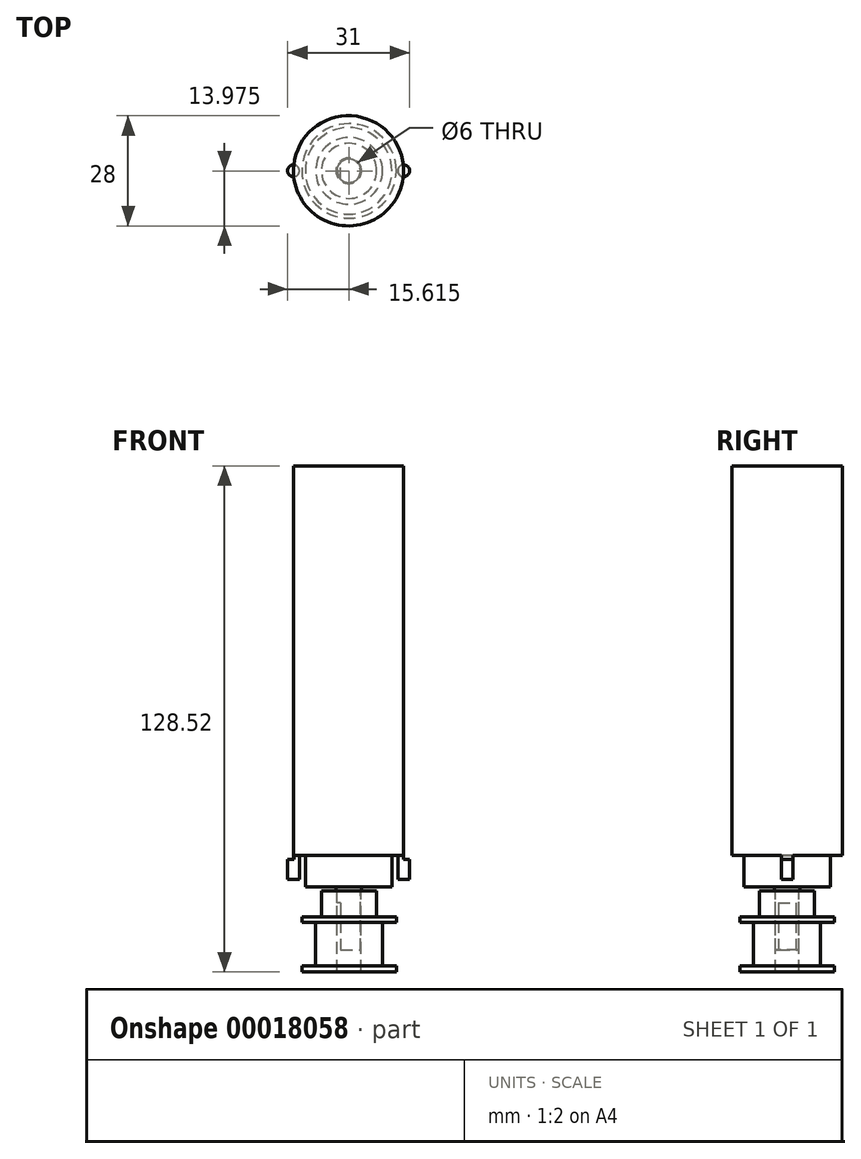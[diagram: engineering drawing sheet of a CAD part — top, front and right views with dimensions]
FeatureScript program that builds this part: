
annotation { "Feature Type Name" : "Feature", "Feature Type Description" : "" }
export const myFeature = defineFeature(function(context is Context, id is Id, definition is map)
    precondition{}
    {
        {
            var Q0;
            Q0=qCreatedBy(makeId("Top.planeOp"),FACE);
            var sketch = newSketch(context, id + "F0", { "sketchPlane" : qUnion([Q0])});
            skCircle(sketch, "E0", {"center": v(0, 0) * mm, "radius": 14 * mm});
            skCircle(sketch, "E1", {"center": v(0, 0) * mm, "radius": 18 * mm});
            skCircle(sketch, "E2", {"center": v(0, 0) * mm, "radius": 11 * mm});
            skCircle(sketch, "E3", {"center": v(0, 0) * mm, "radius": 3 * mm});
            skSolve(sketch);
        }
        {
            var Q0;
            Q0=makeQuery(id+"F0.imprint","IMPRINT",FACE,{"disambiguationData":[TD([[makeQuery(id+"F0.imprint","IMPRINT",EDGE,{"derivedFrom":sQuery(id+"F0.wireOp",EDGE,"E0")}),-1.0]])]});
            var Q1;
            Q1=makeQuery(id+"F0.imprint","IMPRINT",FACE,{"disambiguationData":[TD([[makeQuery(id+"F0.imprint","IMPRINT",EDGE,{"derivedFrom":sQuery(id+"F0.wireOp",EDGE,"E3")}),1.0]])]});
            var Q2;
            Q2=makeQuery(id+"F0.imprint","IMPRINT",FACE,{"disambiguationData":[TD([[makeQuery(id+"F0.imprint","IMPRINT",EDGE,{"derivedFrom":sQuery(id+"F0.wireOp",EDGE,"E0")}),1.0]])]});
            var Q3;
            Q3=makeQuery(id+"F0.imprint","IMPRINT",FACE,{"disambiguationData":[TD([[makeQuery(id+"F0.imprint","IMPRINT",EDGE,{"derivedFrom":sQuery(id+"F0.wireOp",EDGE,"E2")}),1.0]])]});
            extrude(context, id + "F1", {"entities" : qUnion([Q0, Q1, Q2, Q3]), "depth" : 5 * mm});
        }
        {
            var Q0;
            Q0=makeQuery(id+"F1.opExtrude","CAP_FACE",FACE,{"disambiguationData":[OSD([sQuery(id+"F0.wireOp",EDGE,"E1")])],"isStart":false});
            var sketch = newSketch(context, id + "F2", { "sketchPlane" : qUnion([Q0])});
            skCircle(sketch, "E4", {"center": v(0, 0) * mm, "radius": 14 * mm});
            skSolve(sketch);
        }
        {
            var Q0;
            Q0=makeQuery(id+"F2.imprint","IMPRINT",FACE,{"disambiguationData":[TD([[makeQuery(id+"F2.imprint","IMPRINT",EDGE,{"derivedFrom":sQuery(id+"F2.wireOp",EDGE,"E4")}),1.0]])]});
            extrude(context, id + "F3", {"entities" : qUnion([Q0]), "operationType" : NewBodyOperationType.ADD, "depth" : 100 * mm});
        }
        {
            var Q0;
            Q0=makeQuery(id+"F1.opExtrude","CAP_FACE",FACE,{"disambiguationData":[OSD([sQuery(id+"F0.wireOp",EDGE,"E1")])],"isStart":true});
            var sketch = newSketch(context, id + "F4", { "sketchPlane" : qUnion([Q0])});
            skCircle(sketch, "E5", {"center": v(0, 0) * mm, "radius": 11 * mm});
            skSolve(sketch);
        }
        {
            var Q0;
            Q0=makeQuery(id+"F4.imprint","IMPRINT",FACE,{"disambiguationData":[TD([[makeQuery(id+"F4.imprint","IMPRINT",EDGE,{"derivedFrom":sQuery(id+"F4.wireOp",EDGE,"E5")}),1.0]])]});
            extrude(context, id + "F5", {"entities" : qUnion([Q0]), "operationType" : NewBodyOperationType.ADD, "depth" : 2 * mm});
        }
        {
            var Q0;
            Q0=makeQuery(id+"F5.opExtrude","CAP_FACE",FACE,{"disambiguationData":[OSD([sQuery(id+"F4.wireOp",EDGE,"E5")])],"isStart":false});
            var sketch = newSketch(context, id + "F6", { "sketchPlane" : qUnion([Q0])});
            skCircle(sketch, "E6", {"center": v(0, 0) * mm, "radius": 3 * mm});
            skSolve(sketch);
        }
        {
            var Q0;
            Q0=makeQuery(id+"F6.imprint","IMPRINT",FACE,{"disambiguationData":[TD([[makeQuery(id+"F6.imprint","IMPRINT",EDGE,{"derivedFrom":sQuery(id+"F6.wireOp",EDGE,"E6")}),1.0]])]});
            extrude(context, id + "F7", {"entities" : qUnion([Q0]), "operationType" : NewBodyOperationType.ADD, "depth" : 16 * mm});
        }
        {
            var Q0;
            Q0=makeQuery(id+"F7.opExtrude","CAP_FACE",FACE,{"disambiguationData":[OSD([sQuery(id+"F6.wireOp",EDGE,"E6")])],"isStart":false});
            var sketch = newSketch(context, id + "F8", { "sketchPlane" : qUnion([Q0])});
            skLineSegment(sketch, "E7", {"start": v(-2, 2.24) * mm, "end": v(-2, -2.24) * mm});
            skSolve(sketch);
        }
        {
            var Q0;
            {var subQ1=sQuery(id+"F8.wireOp",EDGE,"E7");Q0=makeQuery(id+"F8.imprint","IMPRINT",FACE,{"disambiguationData":[TD([[makeQuery(id+"F8.imprint","IMPRINT",EDGE,{"derivedFrom":subQ1}),-1.0]])]});}
            extrude(context, id + "F9", {"entities" : qUnion([Q0]), "operationType" : NewBodyOperationType.REMOVE, "oppositeDirection" : true, "depth" : 12 * mm});
        }
        {
            var Q0;
            Q0=makeQuery(id+"F5.opExtrude","CAP_FACE",FACE,{"disambiguationData":[OSD([sQuery(id+"F4.wireOp",EDGE,"E5")])],"isStart":false});
            var sketch = newSketch(context, id + "F10", { "sketchPlane" : qUnion([Q0])});
            skCircle(sketch, "E8", {"center": v(-45.71, 18.6) * mm, "radius": 7 * mm});
            skCircle(sketch, "E9", {"center": v(-45.71, 18.6) * mm, "radius": 3 * mm});
            skSolve(sketch);
        }
        {
            var Q0;
            Q0=makeQuery(id+"F10.imprint","IMPRINT",FACE,{"disambiguationData":[TD([[makeQuery(id+"F10.imprint","IMPRINT",EDGE,{"derivedFrom":sQuery(id+"F10.wireOp",EDGE,"E8")}),1.0]])]});
            extrude(context, id + "F11", {"entities" : qUnion([Q0]), "depth" : 6.5 * mm});
        }
        {
            var Q0;
            Q0=makeQuery(id+"F11.opExtrude","CAP_FACE",FACE,{"disambiguationData":[OSD([sQuery(id+"F10.wireOp",EDGE,"E8")])],"isStart":false});
            var sketch = newSketch(context, id + "F12", { "sketchPlane" : qUnion([Q0])});
            skCircle(sketch, "E10", {"center": v(-45.71, 18.6) * mm, "radius": 12 * mm});
            skSolve(sketch);
        }
        {
            var Q0;
            Q0=makeQuery(id+"F12.imprint","IMPRINT",FACE,{"disambiguationData":[TD([[makeQuery(id+"F12.imprint","IMPRINT",EDGE,{"derivedFrom":sQuery(id+"F12.wireOp",EDGE,"E10")}),1.0]])]});
            var Q1;
            Q1=makeQuery(id+"F12.imprint","IMPRINT",FACE,{"disambiguationData":[TD([[makeQuery(id+"F12.imprint","IMPRINT",EDGE,{"derivedFrom":makeQuery(id+"F11.opExtrude","CAP_EDGE",EDGE,{"disambiguationData":[OSD([sQuery(id+"F10.wireOp",EDGE,"E8")])],"isStart":false})}),1.0]])]});
            extrude(context, id + "F13", {"entities" : qUnion([Q0, Q1]), "operationType" : NewBodyOperationType.ADD, "depth" : 1.5 * mm});
        }
        {
            var Q0;
            Q0=makeQuery(id+"F13.opExtrude","CAP_FACE",FACE,{"disambiguationData":[OSD([sQuery(id+"F10.wireOp",EDGE,"E9"),sQuery(id+"F12.wireOp",EDGE,"E10")])],"isStart":false});
            var sketch = newSketch(context, id + "F14", { "sketchPlane" : qUnion([Q0])});
            skCircle(sketch, "E11", {"center": v(-45.71, 18.6) * mm, "radius": 8.5 * mm});
            skSolve(sketch);
        }
        {
            var Q0;
            Q0=makeQuery(id+"F14.imprint","IMPRINT",FACE,{"disambiguationData":[TD([[makeQuery(id+"F14.imprint","IMPRINT",EDGE,{"derivedFrom":sQuery(id+"F14.wireOp",EDGE,"E11")}),1.0]])]});
            extrude(context, id + "F15", {"entities" : qUnion([Q0]), "operationType" : NewBodyOperationType.ADD, "depth" : 11 * mm});
        }
        {
            var Q0;
            Q0=makeQuery(id+"F15.opExtrude","CAP_FACE",FACE,{"disambiguationData":[OSD([sQuery(id+"F10.wireOp",EDGE,"E9"),sQuery(id+"F14.wireOp",EDGE,"E11")])],"isStart":false});
            var sketch = newSketch(context, id + "F16", { "sketchPlane" : qUnion([Q0])});
            skCircle(sketch, "E12", {"center": v(-45.71, 18.6) * mm, "radius": 12 * mm});
            skSolve(sketch);
        }
        {
            var Q0;
            Q0=makeQuery(id+"F16.imprint","IMPRINT",FACE,{"disambiguationData":[TD([[makeQuery(id+"F16.imprint","IMPRINT",EDGE,{"derivedFrom":sQuery(id+"F16.wireOp",EDGE,"E12")}),1.0]])]});
            var Q1;
            Q1=makeQuery(id+"F16.imprint","IMPRINT",FACE,{"disambiguationData":[TD([[makeQuery(id+"F16.imprint","IMPRINT",EDGE,{"derivedFrom":makeQuery(id+"F15.opExtrude","CAP_EDGE",EDGE,{"disambiguationData":[OSD([sQuery(id+"F14.wireOp",EDGE,"E11")])],"isStart":false})}),1.0]])]});
            extrude(context, id + "F17", {"entities" : qUnion([Q0, Q1]), "operationType" : NewBodyOperationType.ADD, "depth" : 1.5 * mm});
        }
        {
            var Q0;
            Q0=makeQuery(id+"F5.opExtrude","CAP_FACE",FACE,{"disambiguationData":[OSD([sQuery(id+"F4.wireOp",EDGE,"E5")])],"isStart":false});
            var sketch = newSketch(context, id + "F18", { "sketchPlane" : qUnion([Q0])});
            skCircle(sketch, "E13", {"center": v(0, 0) * mm, "radius": 3.25 * mm});
            skSolve(sketch);
        }
        {
            var Q0;
            Q0 = qSketchRegion(id + "F18", true);
            extrude(context, id + "F19", {"entities" : qUnion([Q0]), "operationType" : NewBodyOperationType.ADD, "depth" : 1 * mm});
        }
        {
            var Q0;
            Q0=makeQuery(id+"F11.opExtrude","SWEPT_BODY",BODY,{"disambiguationData":[OSD([sQuery(id+"F10.wireOp",EDGE,"E8"),sQuery(id+"F10.wireOp",EDGE,"E9")])]});
            transform(context, id + "F20", {"entities" : qUnion([Q0]), "transformType" : TransformType.TRANSLATION_3D, "dx" : 45.83 * mm, "dy" : 18.58 * mm, "dz" : -1.02 * mm, "makeCopy" : true});
        }
        {
            var Q0;
            Q0=makeQuery(id+"F11.opExtrude","SWEPT_BODY",BODY,{"disambiguationData":[OSD([sQuery(id+"F10.wireOp",EDGE,"E8"),sQuery(id+"F10.wireOp",EDGE,"E9")])]});
            deleteBodies(context, id + "F21", {"entities" : qUnion([Q0])});
        }
        {
            var Q0;
            Q0=makeQuery(id+"F1.opExtrude","CAP_FACE",FACE,{"disambiguationData":[OSD([sQuery(id+"F0.wireOp",EDGE,"E1")])],"isStart":true});
            var sketch = newSketch(context, id + "F22", { "sketchPlane" : qUnion([Q0])});
            skCircle(sketch, "E14", {"center": v(0, 0) * mm, "radius": 14 * mm});
            skCircle(sketch, "E15", {"center": v(0, 14) * mm, "radius": 1.5 * mm});
            skCircle(sketch, "E16", {"center": v(14, 0) * mm, "radius": 1.5 * mm});
            skCircle(sketch, "E17", {"center": v(-14, 0) * mm, "radius": 1.5 * mm});
            skCircle(sketch, "E18", {"center": v(0, -14) * mm, "radius": 1.5 * mm});
            skSolve(sketch);
        }
        {
            var Q0;
            {var subQ0=sQuery(id+"F22.wireOp",EDGE,"E18");var subQ1=sQuery(id+"F22.wireOp",EDGE,"E14");var subQ3=makeQuery(id+"F22.imprint","INTERSECT",VERTEX,{"disambiguationData":[OD(0.0)],"derivedFrom":[subQ1,subQ0]});Q0=makeQuery(id+"F22.imprint","IMPRINT",FACE,{"disambiguationData":[TD([[makeQuery(id+"F22.imprint","IMPRINT",EDGE,{"disambiguationData":[TD([[subQ3,-1.0]])],"derivedFrom":subQ1}),-1.0]])]});}
            var Q1;
            {var subQ0=sQuery(id+"F22.wireOp",EDGE,"E18");var subQ1=sQuery(id+"F22.wireOp",EDGE,"E14");var subQ3=makeQuery(id+"F22.imprint","INTERSECT",VERTEX,{"disambiguationData":[OD(0.0)],"derivedFrom":[subQ1,subQ0]});Q1=makeQuery(id+"F22.imprint","IMPRINT",FACE,{"disambiguationData":[TD([[makeQuery(id+"F22.imprint","IMPRINT",EDGE,{"disambiguationData":[TD([[subQ3,-1.0]])],"derivedFrom":subQ1}),1.0]])]});}
            var Q2;
            {var subQ0=sQuery(id+"F22.wireOp",EDGE,"E16");var subQ1=sQuery(id+"F22.wireOp",EDGE,"E14");var subQ3=makeQuery(id+"F22.imprint","INTERSECT",VERTEX,{"disambiguationData":[OD(0.0)],"derivedFrom":[subQ1,subQ0]});Q2=makeQuery(id+"F22.imprint","IMPRINT",FACE,{"disambiguationData":[TD([[makeQuery(id+"F22.imprint","IMPRINT",EDGE,{"disambiguationData":[TD([[subQ3,1.0]])],"derivedFrom":subQ1}),1.0]])]});}
            var Q3;
            {var subQ0=sQuery(id+"F22.wireOp",EDGE,"E16");var subQ1=sQuery(id+"F22.wireOp",EDGE,"E14");var subQ3=makeQuery(id+"F22.imprint","INTERSECT",VERTEX,{"disambiguationData":[OD(0.0)],"derivedFrom":[subQ1,subQ0]});Q3=makeQuery(id+"F22.imprint","IMPRINT",FACE,{"disambiguationData":[TD([[makeQuery(id+"F22.imprint","IMPRINT",EDGE,{"disambiguationData":[TD([[subQ3,1.0]])],"derivedFrom":subQ1}),-1.0]])]});}
            var Q4;
            {var subQ0=sQuery(id+"F22.wireOp",EDGE,"E15");var subQ1=sQuery(id+"F22.wireOp",EDGE,"E14");var subQ3=makeQuery(id+"F22.imprint","INTERSECT",VERTEX,{"disambiguationData":[OD(0.0)],"derivedFrom":[subQ1,subQ0]});Q4=makeQuery(id+"F22.imprint","IMPRINT",FACE,{"disambiguationData":[TD([[makeQuery(id+"F22.imprint","IMPRINT",EDGE,{"disambiguationData":[TD([[subQ3,-1.0]])],"derivedFrom":subQ1}),1.0]])]});}
            var Q5;
            {var subQ0=sQuery(id+"F22.wireOp",EDGE,"E15");var subQ1=sQuery(id+"F22.wireOp",EDGE,"E14");var subQ3=makeQuery(id+"F22.imprint","INTERSECT",VERTEX,{"disambiguationData":[OD(0.0)],"derivedFrom":[subQ1,subQ0]});Q5=makeQuery(id+"F22.imprint","IMPRINT",FACE,{"disambiguationData":[TD([[makeQuery(id+"F22.imprint","IMPRINT",EDGE,{"disambiguationData":[TD([[subQ3,-1.0]])],"derivedFrom":subQ1}),-1.0]])]});}
            var Q6;
            {var subQ0=sQuery(id+"F22.wireOp",EDGE,"E17");var subQ1=sQuery(id+"F22.wireOp",EDGE,"E14");var subQ3=makeQuery(id+"F22.imprint","INTERSECT",VERTEX,{"disambiguationData":[OD(0.0)],"derivedFrom":[subQ1,subQ0]});Q6=makeQuery(id+"F22.imprint","IMPRINT",FACE,{"disambiguationData":[TD([[makeQuery(id+"F22.imprint","IMPRINT",EDGE,{"disambiguationData":[TD([[subQ3,-1.0]])],"derivedFrom":subQ1}),-1.0]])]});}
            var Q7;
            {var subQ0=sQuery(id+"F22.wireOp",EDGE,"E17");var subQ1=sQuery(id+"F22.wireOp",EDGE,"E14");var subQ3=makeQuery(id+"F22.imprint","INTERSECT",VERTEX,{"disambiguationData":[OD(0.0)],"derivedFrom":[subQ1,subQ0]});Q7=makeQuery(id+"F22.imprint","IMPRINT",FACE,{"disambiguationData":[TD([[makeQuery(id+"F22.imprint","IMPRINT",EDGE,{"disambiguationData":[TD([[subQ3,-1.0]])],"derivedFrom":subQ1}),1.0]])]});}
            var Q8;
            Q8=sQuery(id+"F22.wireOp",EDGE,"E18");
            var Q9;
            Q9=sQuery(id+"F22.wireOp",EDGE,"E17");
            var Q10;
            Q10=sQuery(id+"F22.wireOp",EDGE,"E15");
            var Q11;
            Q11=sQuery(id+"F22.wireOp",EDGE,"E16");
            extrude(context, id + "F23", {"entities" : qUnion([Q0, Q1, Q2, Q3, Q4, Q5, Q6, Q7]), "operationType" : NewBodyOperationType.REMOVE, "surfaceEntities" : qUnion([Q8, Q9, Q10, Q11]), "oppositeDirection" : true, "depth" : 6 * mm});
        }
    });
